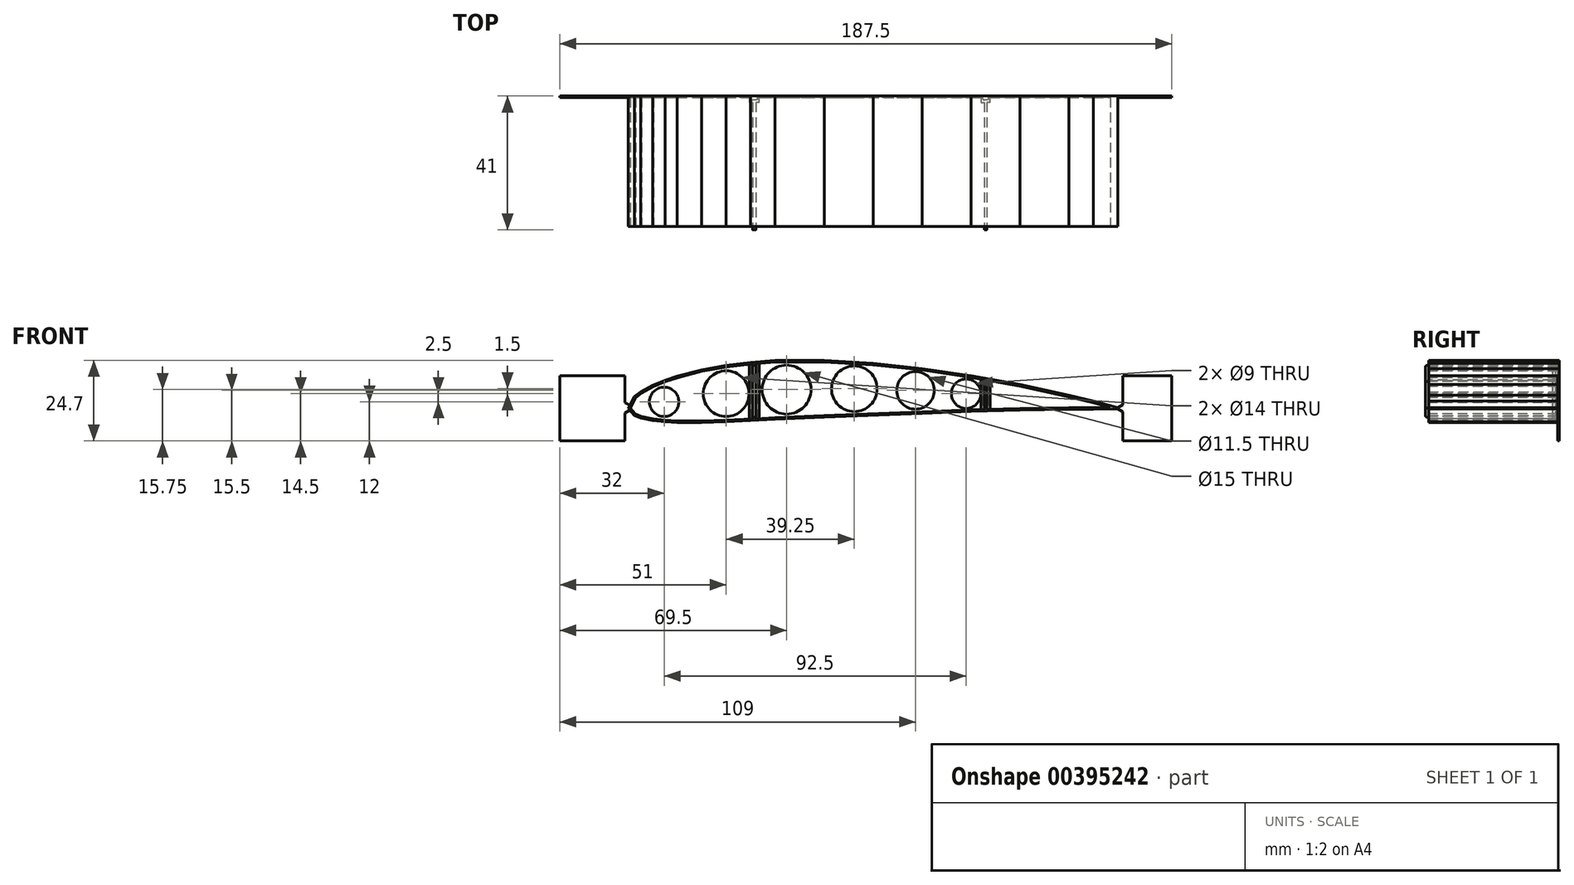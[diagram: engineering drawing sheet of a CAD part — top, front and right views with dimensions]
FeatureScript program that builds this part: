
annotation { "Feature Type Name" : "Feature", "Feature Type Description" : "" }
export const myFeature = defineFeature(function(context is Context, id is Id, definition is map)
    precondition{}
    {
        {
            var Q0;
            Q0=qCreatedBy(makeId("Front.planeOp"),FACE);
            var sketch = newSketch(context, id + "F0", { "sketchPlane" : qUnion([Q0])});
            skLineSegment(sketch, "E0", {"start": v(150, 0.2) * mm, "end": v(142.5, 2.2) * mm});
            skLineSegment(sketch, "E1", {"start": v(142.5, 2.2) * mm, "end": v(135, 4.07) * mm});
            skLineSegment(sketch, "E2", {"start": v(135, 4.07) * mm, "end": v(120, 7.34) * mm});
            skLineSegment(sketch, "E3", {"start": v(120, 7.34) * mm, "end": v(105, 10.04) * mm});
            skLineSegment(sketch, "E4", {"start": v(105, 10.03) * mm, "end": v(90, 12.2) * mm});
            skLineSegment(sketch, "E5", {"start": v(90, 12.21) * mm, "end": v(75, 13.79) * mm});
            skLineSegment(sketch, "E6", {"start": v(75, 13.79) * mm, "end": v(60, 14.7) * mm});
            skLineSegment(sketch, "E7", {"start": v(60, 14.7) * mm, "end": v(45, 14.64) * mm});
            skLineSegment(sketch, "E8", {"start": v(45, 14.64) * mm, "end": v(37.5, 14.11) * mm});
            skLineSegment(sketch, "E9", {"start": v(37.5, 14.12) * mm, "end": v(30, 13.2) * mm});
            skLineSegment(sketch, "E10", {"start": v(30, 13.2) * mm, "end": v(22.5, 11.83) * mm});
            skLineSegment(sketch, "E11", {"start": v(22.5, 11.84) * mm, "end": v(15, 9.88) * mm});
            skLineSegment(sketch, "E12", {"start": v(15, 9.88) * mm, "end": v(11.25, 8.64) * mm});
            skLineSegment(sketch, "E13", {"start": v(0, 0) * mm, "end": v(1.88, -2.15) * mm});
            skLineSegment(sketch, "E14", {"start": v(1.87, -2.14) * mm, "end": v(3.75, -2.92) * mm});
            skLineSegment(sketch, "E15", {"start": v(3.75, -2.92) * mm, "end": v(7.5, -3.73) * mm});
            skLineSegment(sketch, "E16", {"start": v(7.5, -3.73) * mm, "end": v(11.25, -4.11) * mm});
            skLineSegment(sketch, "E17", {"start": v(11.25, -4.1) * mm, "end": v(15, -4.3) * mm});
            skLineSegment(sketch, "E18", {"start": v(15, -4.29) * mm, "end": v(22.5, -4.32) * mm});
            skLineSegment(sketch, "E19", {"start": v(22.5, -4.32) * mm, "end": v(30, -4.11) * mm});
            skLineSegment(sketch, "E20", {"start": v(30, -4.11) * mm, "end": v(37.5, -3.75) * mm});
            skLineSegment(sketch, "E21", {"start": v(37.5, -3.75) * mm, "end": v(45, -3.39) * mm});
            skLineSegment(sketch, "E22", {"start": v(45, -3.39) * mm, "end": v(60, -2.7) * mm});
            skLineSegment(sketch, "E23", {"start": v(60, -2.7) * mm, "end": v(75, -2.1) * mm});
            skLineSegment(sketch, "E24", {"start": v(75, -2.1) * mm, "end": v(90, -1.5) * mm});
            skLineSegment(sketch, "E25", {"start": v(11.25, 8.64) * mm, "end": v(7.5, 7.1) * mm});
            skLineSegment(sketch, "E26", {"start": v(7.5, 7.1) * mm, "end": v(3.75, 5.08) * mm});
            skLineSegment(sketch, "E27", {"start": v(3.75, 5.08) * mm, "end": v(1.88, 3.66) * mm});
            skLineSegment(sketch, "E28", {"start": v(1.88, 3.66) * mm, "end": v(0, 0) * mm});
            skLineSegment(sketch, "E29", {"start": v(90, -1.5) * mm, "end": v(105, -0.97) * mm});
            skLineSegment(sketch, "E30", {"start": v(105, -0.97) * mm, "end": v(120, -0.58) * mm});
            skLineSegment(sketch, "E31", {"start": v(120, -0.58) * mm, "end": v(135, -0.33) * mm});
            skLineSegment(sketch, "E32", {"start": v(135, -0.33) * mm, "end": v(142.5, -0.24) * mm});
            skLineSegment(sketch, "E33", {"start": v(142.5, -0.24) * mm, "end": v(150, -0.2) * mm});
            skLineSegment(sketch, "E34", {"start": v(150, -0.2) * mm, "end": v(150, 0.2) * mm});
            skSolve(sketch);
        }
        {
            var Q0;
            Q0=makeQuery(id+"F0.imprint","IMPRINT",FACE,{"disambiguationData":[TD([[makeQuery(id+"F0.imprint","IMPRINT",EDGE,{"derivedFrom":sQuery(id+"F0.wireOp",EDGE,"E0")}),1.0]])]});
            extrude(context, id + "F1", {"entities" : qUnion([Q0]), "depth" : 40 * mm});
        }
        {
            var Q0;
            Q0=makeQuery(id+"F1.opExtrude","CAP_FACE",FACE,{"disambiguationData":[OSD([sQuery(id+"F0.wireOp",EDGE,"E0"),sQuery(id+"F0.wireOp",EDGE,"E1"),sQuery(id+"F0.wireOp",EDGE,"E2"),sQuery(id+"F0.wireOp",EDGE,"E3"),sQuery(id+"F0.wireOp",EDGE,"E4"),sQuery(id+"F0.wireOp",EDGE,"E5"),sQuery(id+"F0.wireOp",EDGE,"E6"),sQuery(id+"F0.wireOp",EDGE,"E7"),sQuery(id+"F0.wireOp",EDGE,"E8"),sQuery(id+"F0.wireOp",EDGE,"E9"),sQuery(id+"F0.wireOp",EDGE,"E10"),sQuery(id+"F0.wireOp",EDGE,"E11"),sQuery(id+"F0.wireOp",EDGE,"E12"),sQuery(id+"F0.wireOp",EDGE,"E13"),sQuery(id+"F0.wireOp",EDGE,"E14"),sQuery(id+"F0.wireOp",EDGE,"E15"),sQuery(id+"F0.wireOp",EDGE,"E16"),sQuery(id+"F0.wireOp",EDGE,"E17"),sQuery(id+"F0.wireOp",EDGE,"E18"),sQuery(id+"F0.wireOp",EDGE,"E19"),sQuery(id+"F0.wireOp",EDGE,"E20"),sQuery(id+"F0.wireOp",EDGE,"E21"),sQuery(id+"F0.wireOp",EDGE,"E22"),sQuery(id+"F0.wireOp",EDGE,"E23"),sQuery(id+"F0.wireOp",EDGE,"E24"),sQuery(id+"F0.wireOp",EDGE,"E25"),sQuery(id+"F0.wireOp",EDGE,"E26"),sQuery(id+"F0.wireOp",EDGE,"E27"),sQuery(id+"F0.wireOp",EDGE,"E28"),sQuery(id+"F0.wireOp",EDGE,"E29"),sQuery(id+"F0.wireOp",EDGE,"E30"),sQuery(id+"F0.wireOp",EDGE,"E31"),sQuery(id+"F0.wireOp",EDGE,"E32"),sQuery(id+"F0.wireOp",EDGE,"E33"),sQuery(id+"F0.wireOp",EDGE,"E34")])],"isStart":false});
            var sketch = newSketch(context, id + "F2", { "sketchPlane" : qUnion([Q0])});
            skLineSegment(sketch, "E35.0", {"start": v(119.99, -0.09) * mm, "end": v(135, 0.17) * mm});
            skLineSegment(sketch, "E35.1", {"start": v(104.98, -0.48) * mm, "end": v(109.1, -0.37) * mm});
            skLineSegment(sketch, "E35.2", {"start": v(89.98, -1) * mm, "end": v(104.98, -0.48) * mm});
            skLineSegment(sketch, "E35.3", {"start": v(59.98, -2.2) * mm, "end": v(89.98, -1) * mm});
            skLineSegment(sketch, "E35.4", {"start": v(44.98, -2.9) * mm, "end": v(59.98, -2.2) * mm});
            skLineSegment(sketch, "E35.5", {"start": v(29.98, -3.61) * mm, "end": v(38.1, -3.22) * mm});
            skLineSegment(sketch, "E35.6", {"start": v(22.5, -3.82) * mm, "end": v(29.98, -3.61) * mm});
            skLineSegment(sketch, "E35.7", {"start": v(15.01, -3.8) * mm, "end": v(22.5, -3.82) * mm});
            skLineSegment(sketch, "E35.8", {"start": v(11.29, -3.61) * mm, "end": v(15.01, -3.8) * mm});
            skLineSegment(sketch, "E35.9", {"start": v(45.02, 14.14) * mm, "end": v(39.1, 13.73) * mm});
            skLineSegment(sketch, "E35.10", {"start": v(59.99, 14.2) * mm, "end": v(45.02, 14.14) * mm});
            skLineSegment(sketch, "E35.11", {"start": v(74.96, 13.29) * mm, "end": v(59.99, 14.2) * mm});
            skLineSegment(sketch, "E35.12", {"start": v(89.94, 11.71) * mm, "end": v(74.96, 13.29) * mm});
            skLineSegment(sketch, "E35.13", {"start": v(104.92, 9.54) * mm, "end": v(89.94, 11.71) * mm});
            skLineSegment(sketch, "E35.14", {"start": v(119.9, 6.84) * mm, "end": v(109.85, 8.65) * mm});
            skLineSegment(sketch, "E35.15", {"start": v(142.5, 0.26) * mm, "end": v(147.7, 0.3) * mm});
            skLineSegment(sketch, "E35.16", {"start": v(147.7, 0.3) * mm, "end": v(142.38, 1.72) * mm});
            skLineSegment(sketch, "E35.17", {"start": v(142.38, 1.72) * mm, "end": v(134.89, 3.58) * mm});
            skLineSegment(sketch, "E35.18", {"start": v(134.89, 3.58) * mm, "end": v(119.9, 6.84) * mm});
            skLineSegment(sketch, "E35.19", {"start": v(37.55, 13.62) * mm, "end": v(30.08, 12.7) * mm});
            skLineSegment(sketch, "E35.20", {"start": v(30.08, 12.7) * mm, "end": v(22.6, 11.35) * mm});
            skLineSegment(sketch, "E35.21", {"start": v(22.6, 11.35) * mm, "end": v(15.14, 9.4) * mm});
            skLineSegment(sketch, "E35.22", {"start": v(15.14, 9.4) * mm, "end": v(11.42, 8.17) * mm});
            skLineSegment(sketch, "E35.23", {"start": v(11.42, 8.17) * mm, "end": v(7.71, 6.64) * mm});
            skLineSegment(sketch, "E35.24", {"start": v(7.71, 6.64) * mm, "end": v(4.02, 4.66) * mm});
            skLineSegment(sketch, "E35.25", {"start": v(4.02, 4.66) * mm, "end": v(2.27, 3.33) * mm});
            skLineSegment(sketch, "E35.26", {"start": v(2.27, 3.33) * mm, "end": v(0.6, 0.07) * mm});
            skLineSegment(sketch, "E35.27", {"start": v(0.6, 0.07) * mm, "end": v(2.17, -1.73) * mm});
            skLineSegment(sketch, "E35.28", {"start": v(135, 0.17) * mm, "end": v(142.5, 0.26) * mm});
            skLineSegment(sketch, "E35.29", {"start": v(2.17, -1.73) * mm, "end": v(3.9, -2.45) * mm});
            skLineSegment(sketch, "E35.30", {"start": v(3.9, -2.45) * mm, "end": v(7.58, -3.24) * mm});
            skLineSegment(sketch, "E35.31", {"start": v(7.58, -3.24) * mm, "end": v(11.29, -3.61) * mm});
            skLineSegment(sketch, "E36", {"start": v(0.6, 0.07) * mm, "end": v(38.1, 0.07) * mm, "construction": true});
            skLineSegment(sketch, "E37", {"start": v(38.1, -3.22) * mm, "end": v(38.1, 13.66) * mm});
            skLineSegment(sketch, "E38", {"start": v(39.1, -3.17) * mm, "end": v(39.1, 13.73) * mm});
            skLineSegment(sketch, "E39.trimOffspring", {"start": v(38.1, 13.66) * mm, "end": v(37.55, 13.62) * mm});
            skLineSegment(sketch, "E40.trimOffspring", {"start": v(39.1, -3.17) * mm, "end": v(44.98, -2.9) * mm});
            skLineSegment(sketch, "E41", {"start": v(39.1, 0) * mm, "end": v(109.1, 1.2) * mm, "construction": true});
            skLineSegment(sketch, "E42", {"start": v(109.1, 8.79) * mm, "end": v(109.1, -0.37) * mm});
            skLineSegment(sketch, "E43", {"start": v(109.85, -0.35) * mm, "end": v(109.85, 8.65) * mm});
            skLineSegment(sketch, "E44.trimOffspring", {"start": v(109.1, 8.79) * mm, "end": v(104.92, 9.54) * mm});
            skLineSegment(sketch, "E45.trimOffspring", {"start": v(109.85, -0.35) * mm, "end": v(119.99, -0.09) * mm});
            skSolve(sketch);
        }
        {
            var Q0;
            Q0=makeQuery(id+"F2.imprint","IMPRINT",FACE,{"disambiguationData":[TD([[makeQuery(id+"F2.imprint","IMPRINT",EDGE,{"derivedFrom":sQuery(id+"F2.wireOp",EDGE,"E35.5")}),1.0]])]});
            var Q1;
            Q1=makeQuery(id+"F2.imprint","IMPRINT",FACE,{"disambiguationData":[TD([[makeQuery(id+"F2.imprint","IMPRINT",EDGE,{"derivedFrom":sQuery(id+"F2.wireOp",EDGE,"E35.1")}),1.0]])]});
            var Q2;
            Q2=makeQuery(id+"F2.imprint","IMPRINT",FACE,{"disambiguationData":[TD([[makeQuery(id+"F2.imprint","IMPRINT",EDGE,{"derivedFrom":sQuery(id+"F2.wireOp",EDGE,"E35.0")}),1.0]])]});
            extrude(context, id + "F3", {"entities" : qUnion([Q0, Q1, Q2]), "operationType" : NewBodyOperationType.REMOVE, "oppositeDirection" : true, "depth" : 39.5 * mm});
        }
        {
            var Q0;
            Q0=makeQuery(id+"F3.boolean.opBoolean","COPY",FACE,{"derivedFrom":makeQuery(id+"F3.opExtrude","CAP_FACE",FACE,{"disambiguationData":[OSD([sQuery(id+"F2.wireOp",EDGE,"E35.1"),sQuery(id+"F2.wireOp",EDGE,"E35.2"),sQuery(id+"F2.wireOp",EDGE,"E35.3"),sQuery(id+"F2.wireOp",EDGE,"E35.4"),sQuery(id+"F2.wireOp",EDGE,"E35.9"),sQuery(id+"F2.wireOp",EDGE,"E35.10"),sQuery(id+"F2.wireOp",EDGE,"E35.11"),sQuery(id+"F2.wireOp",EDGE,"E35.12"),sQuery(id+"F2.wireOp",EDGE,"E35.13"),sQuery(id+"F2.wireOp",EDGE,"E38"),sQuery(id+"F2.wireOp",EDGE,"E40.trimOffspring"),sQuery(id+"F2.wireOp",EDGE,"E42"),sQuery(id+"F2.wireOp",EDGE,"E44.trimOffspring")])],"isStart":false})});
            var sketch = newSketch(context, id + "F4", { "sketchPlane" : qUnion([Q0])});
            skCircle(sketch, "E46", {"center": v(48.5, 5.75) * mm, "radius": 7.5 * mm});
            skCircle(sketch, "E47", {"center": v(69.25, 6) * mm, "radius": 7 * mm});
            skCircle(sketch, "E48", {"center": v(88, 5.5) * mm, "radius": 5.75 * mm});
            skCircle(sketch, "E49", {"center": v(103.5, 4.5) * mm, "radius": 4.5 * mm});
            skCircle(sketch, "E50", {"center": v(30, 4.5) * mm, "radius": 7 * mm});
            skCircle(sketch, "E51", {"center": v(11, 2) * mm, "radius": 4.5 * mm});
            skSolve(sketch);
        }
        {
            var Q0;
            Q0=makeQuery(id+"F4.imprint","IMPRINT",FACE,{"disambiguationData":[TD([[makeQuery(id+"F4.imprint","IMPRINT",EDGE,{"derivedFrom":sQuery(id+"F4.wireOp",EDGE,"E51")}),1.0]])]});
            var Q1;
            Q1=makeQuery(id+"F4.imprint","IMPRINT",FACE,{"disambiguationData":[TD([[makeQuery(id+"F4.imprint","IMPRINT",EDGE,{"derivedFrom":sQuery(id+"F4.wireOp",EDGE,"E50")}),1.0]])]});
            var Q2;
            Q2=makeQuery(id+"F4.imprint","IMPRINT",FACE,{"disambiguationData":[TD([[makeQuery(id+"F4.imprint","IMPRINT",EDGE,{"derivedFrom":sQuery(id+"F4.wireOp",EDGE,"E46")}),1.0]])]});
            var Q3;
            Q3=makeQuery(id+"F4.imprint","IMPRINT",FACE,{"disambiguationData":[TD([[makeQuery(id+"F4.imprint","IMPRINT",EDGE,{"derivedFrom":sQuery(id+"F4.wireOp",EDGE,"E47")}),1.0]])]});
            var Q4;
            Q4=makeQuery(id+"F4.imprint","IMPRINT",FACE,{"disambiguationData":[TD([[makeQuery(id+"F4.imprint","IMPRINT",EDGE,{"derivedFrom":sQuery(id+"F4.wireOp",EDGE,"E48")}),1.0]])]});
            var Q5;
            Q5=makeQuery(id+"F4.imprint","IMPRINT",FACE,{"disambiguationData":[TD([[makeQuery(id+"F4.imprint","IMPRINT",EDGE,{"derivedFrom":sQuery(id+"F4.wireOp",EDGE,"E49")}),1.0]])]});
            extrude(context, id + "F5", {"entities" : qUnion([Q0, Q1, Q2, Q3, Q4, Q5]), "operationType" : NewBodyOperationType.REMOVE, "endBound" : BoundingType.THROUGH_ALL, "oppositeDirection" : true, "depth" : 25 * mm});
        }
        {
            var Q0;
            Q0=makeQuery(id+"F1.opExtrude","CAP_FACE",FACE,{"disambiguationData":[OSD([sQuery(id+"F0.wireOp",EDGE,"E0"),sQuery(id+"F0.wireOp",EDGE,"E1"),sQuery(id+"F0.wireOp",EDGE,"E2"),sQuery(id+"F0.wireOp",EDGE,"E3"),sQuery(id+"F0.wireOp",EDGE,"E4"),sQuery(id+"F0.wireOp",EDGE,"E5"),sQuery(id+"F0.wireOp",EDGE,"E6"),sQuery(id+"F0.wireOp",EDGE,"E7"),sQuery(id+"F0.wireOp",EDGE,"E8"),sQuery(id+"F0.wireOp",EDGE,"E9"),sQuery(id+"F0.wireOp",EDGE,"E10"),sQuery(id+"F0.wireOp",EDGE,"E11"),sQuery(id+"F0.wireOp",EDGE,"E12"),sQuery(id+"F0.wireOp",EDGE,"E13"),sQuery(id+"F0.wireOp",EDGE,"E14"),sQuery(id+"F0.wireOp",EDGE,"E15"),sQuery(id+"F0.wireOp",EDGE,"E16"),sQuery(id+"F0.wireOp",EDGE,"E17"),sQuery(id+"F0.wireOp",EDGE,"E18"),sQuery(id+"F0.wireOp",EDGE,"E19"),sQuery(id+"F0.wireOp",EDGE,"E20"),sQuery(id+"F0.wireOp",EDGE,"E21"),sQuery(id+"F0.wireOp",EDGE,"E22"),sQuery(id+"F0.wireOp",EDGE,"E23"),sQuery(id+"F0.wireOp",EDGE,"E24"),sQuery(id+"F0.wireOp",EDGE,"E25"),sQuery(id+"F0.wireOp",EDGE,"E26"),sQuery(id+"F0.wireOp",EDGE,"E27"),sQuery(id+"F0.wireOp",EDGE,"E28"),sQuery(id+"F0.wireOp",EDGE,"E29"),sQuery(id+"F0.wireOp",EDGE,"E30"),sQuery(id+"F0.wireOp",EDGE,"E31"),sQuery(id+"F0.wireOp",EDGE,"E32"),sQuery(id+"F0.wireOp",EDGE,"E33"),sQuery(id+"F0.wireOp",EDGE,"E34")])],"isStart":true});
            var sketch = newSketch(context, id + "F6", { "sketchPlane" : qUnion([Q0])});
            skLineSegment(sketch, "E52.left", {"start": v(-37.1, 14.07) * mm, "end": v(-37.1, -3.77) * mm});
            skLineSegment(sketch, "E52.right", {"start": v(-40.1, 14.3) * mm, "end": v(-40.1, -3.63) * mm});
            skLineSegment(sketch, "E53.left", {"start": v(-108.1, 9.48) * mm, "end": v(-108.1, -0.9) * mm});
            skLineSegment(sketch, "E53.right", {"start": v(-110.85, 8.98) * mm, "end": v(-110.85, -0.82) * mm});
            skLineSegment(sketch, "E54", {"start": v(-40.1, 14.3) * mm, "end": v(-37.5, 14.11) * mm});
            skLineSegment(sketch, "E55", {"start": v(-37.5, 14.12) * mm, "end": v(-37.1, 14.07) * mm});
            skLineSegment(sketch, "E56", {"start": v(-37.1, -3.77) * mm, "end": v(-40.1, -3.63) * mm});
            skLineSegment(sketch, "E57", {"start": v(-110.85, 8.98) * mm, "end": v(-108.1, 9.48) * mm});
            skLineSegment(sketch, "E58", {"start": v(-108.1, -0.9) * mm, "end": v(-110.85, -0.82) * mm});
            skSolve(sketch);
        }
        {
            var Q0;
            Q0=makeQuery(id+"F6.imprint","IMPRINT",FACE,{"disambiguationData":[TD([[makeQuery(id+"F6.imprint","IMPRINT",EDGE,{"derivedFrom":sQuery(id+"F6.wireOp",EDGE,"E53.left")}),-1.0]])]});
            var Q1;
            Q1=makeQuery(id+"F6.imprint","IMPRINT",FACE,{"disambiguationData":[TD([[makeQuery(id+"F6.imprint","IMPRINT",EDGE,{"derivedFrom":sQuery(id+"F6.wireOp",EDGE,"E52.left")}),-1.0]])]});
            extrude(context, id + "F7", {"entities" : qUnion([Q0, Q1]), "operationType" : NewBodyOperationType.ADD, "oppositeDirection" : true, "depth" : 2 * mm});
        }
        {
            var Q0;
            {var subQ8=sQuery(id+"F6.wireOp",EDGE,"E52.right");Q0=makeQuery(id+"F6.imprint","IMPRINT",FACE,{"disambiguationData":[TD([[makeQuery(id+"F6.imprint","IMPRINT",EDGE,{"derivedFrom":subQ8}),-1.0]])]});}
            var sketch = newSketch(context, id + "F8", { "sketchPlane" : qUnion([Q0])});
            skLineSegment(sketch, "E59.bottom", {"start": v(-110.35, 8.48) * mm, "end": v(-108.6, 8.48) * mm});
            skLineSegment(sketch, "E59.top", {"start": v(-110.35, -0.32) * mm, "end": v(-108.6, -0.32) * mm});
            skLineSegment(sketch, "E59.left", {"start": v(-110.35, 8.48) * mm, "end": v(-110.35, -0.32) * mm});
            skLineSegment(sketch, "E59.right", {"start": v(-108.6, 8.48) * mm, "end": v(-108.6, -0.32) * mm});
            skLineSegment(sketch, "E60.bottom", {"start": v(-39.6, 13.57) * mm, "end": v(-37.6, 13.57) * mm});
            skLineSegment(sketch, "E60.top", {"start": v(-39.6, -3.13) * mm, "end": v(-37.6, -3.13) * mm});
            skLineSegment(sketch, "E60.left", {"start": v(-39.6, 13.57) * mm, "end": v(-39.6, -3.13) * mm});
            skLineSegment(sketch, "E60.right", {"start": v(-37.6, 13.57) * mm, "end": v(-37.6, -3.13) * mm});
            skSolve(sketch);
        }
        {
            var Q0;
            Q0=makeQuery(id+"F8.imprint","IMPRINT",FACE,{"disambiguationData":[TD([[makeQuery(id+"F8.imprint","IMPRINT",EDGE,{"derivedFrom":sQuery(id+"F8.wireOp",EDGE,"E59.bottom")}),-1.0]])]});
            var Q1;
            Q1=makeQuery(id+"F8.imprint","IMPRINT",FACE,{"disambiguationData":[TD([[makeQuery(id+"F8.imprint","IMPRINT",EDGE,{"derivedFrom":sQuery(id+"F8.wireOp",EDGE,"E60.bottom")}),-1.0]])]});
            extrude(context, id + "F9", {"entities" : qUnion([Q0, Q1]), "operationType" : NewBodyOperationType.REMOVE, "oppositeDirection" : true, "depth" : 1.25 * mm});
        }
        {
            var Q0;
            Q0=makeQuery(id+"F9.boolean.opBoolean","COPY",FACE,{"derivedFrom":makeQuery(id+"F9.opExtrude","CAP_FACE",FACE,{"disambiguationData":[OSD([sQuery(id+"F8.wireOp",EDGE,"E60.bottom"),sQuery(id+"F8.wireOp",EDGE,"E60.top"),sQuery(id+"F8.wireOp",EDGE,"E60.left"),sQuery(id+"F8.wireOp",EDGE,"E60.right")])],"isStart":false})});
            var Q1;
            Q1=makeQuery(id+"F9.boolean.opBoolean","COPY",FACE,{"derivedFrom":makeQuery(id+"F9.opExtrude","CAP_FACE",FACE,{"disambiguationData":[OSD([sQuery(id+"F8.wireOp",EDGE,"E59.bottom"),sQuery(id+"F8.wireOp",EDGE,"E59.top"),sQuery(id+"F8.wireOp",EDGE,"E59.left"),sQuery(id+"F8.wireOp",EDGE,"E59.right")])],"isStart":false})});
            fillet(context, id + "F10", {"entities" : qUnion([Q0, Q1]), "radius" : 0.5 * mm, "tangentPropagation" : true, "allowEdgeOverflow" : false});
        }
        {
            var Q0;
            Q0=makeQuery(id+"F1.opExtrude","CAP_FACE",FACE,{"disambiguationData":[OSD([sQuery(id+"F0.wireOp",EDGE,"E0"),sQuery(id+"F0.wireOp",EDGE,"E1"),sQuery(id+"F0.wireOp",EDGE,"E2"),sQuery(id+"F0.wireOp",EDGE,"E3"),sQuery(id+"F0.wireOp",EDGE,"E4"),sQuery(id+"F0.wireOp",EDGE,"E5"),sQuery(id+"F0.wireOp",EDGE,"E6"),sQuery(id+"F0.wireOp",EDGE,"E7"),sQuery(id+"F0.wireOp",EDGE,"E8"),sQuery(id+"F0.wireOp",EDGE,"E9"),sQuery(id+"F0.wireOp",EDGE,"E10"),sQuery(id+"F0.wireOp",EDGE,"E11"),sQuery(id+"F0.wireOp",EDGE,"E12"),sQuery(id+"F0.wireOp",EDGE,"E13"),sQuery(id+"F0.wireOp",EDGE,"E14"),sQuery(id+"F0.wireOp",EDGE,"E15"),sQuery(id+"F0.wireOp",EDGE,"E16"),sQuery(id+"F0.wireOp",EDGE,"E17"),sQuery(id+"F0.wireOp",EDGE,"E18"),sQuery(id+"F0.wireOp",EDGE,"E19"),sQuery(id+"F0.wireOp",EDGE,"E20"),sQuery(id+"F0.wireOp",EDGE,"E21"),sQuery(id+"F0.wireOp",EDGE,"E22"),sQuery(id+"F0.wireOp",EDGE,"E23"),sQuery(id+"F0.wireOp",EDGE,"E24"),sQuery(id+"F0.wireOp",EDGE,"E25"),sQuery(id+"F0.wireOp",EDGE,"E26"),sQuery(id+"F0.wireOp",EDGE,"E27"),sQuery(id+"F0.wireOp",EDGE,"E28"),sQuery(id+"F0.wireOp",EDGE,"E29"),sQuery(id+"F0.wireOp",EDGE,"E30"),sQuery(id+"F0.wireOp",EDGE,"E31"),sQuery(id+"F0.wireOp",EDGE,"E32"),sQuery(id+"F0.wireOp",EDGE,"E33"),sQuery(id+"F0.wireOp",EDGE,"E34")])],"isStart":false});
            var sketch = newSketch(context, id + "F11", { "sketchPlane" : qUnion([Q0])});
            skLineSegment(sketch, "E61.bottom", {"start": v(39.1, 13.16) * mm, "end": v(38.1, 13.16) * mm});
            skLineSegment(sketch, "E61.top", {"start": v(39.1, -2.67) * mm, "end": v(38.1, -2.67) * mm});
            skLineSegment(sketch, "E61.left", {"start": v(39.1, 13.16) * mm, "end": v(39.1, -2.67) * mm});
            skLineSegment(sketch, "E61.right", {"start": v(38.1, 13.16) * mm, "end": v(38.1, -2.67) * mm});
            skLineSegment(sketch, "E62.bottom", {"start": v(109.85, 8.16) * mm, "end": v(109.1, 8.16) * mm});
            skLineSegment(sketch, "E62.top", {"start": v(109.85, 0.15) * mm, "end": v(109.1, 0.15) * mm});
            skLineSegment(sketch, "E62.left", {"start": v(109.85, 8.16) * mm, "end": v(109.85, 0.15) * mm});
            skLineSegment(sketch, "E62.right", {"start": v(109.1, 8.16) * mm, "end": v(109.1, 0.15) * mm});
            skPoint(sketch, "E63", {"position": v(109.85, 9.16) * mm});
            skPoint(sketch, "E64", {"position": v(109.85, -0.85) * mm});
            skPoint(sketch, "E65", {"position": v(38.1, 14.16) * mm});
            skPoint(sketch, "E66", {"position": v(39.1, -3.67) * mm});
            skSolve(sketch);
        }
        {
            var Q0;
            Q0=makeQuery(id+"F11.imprint","IMPRINT",FACE,{"disambiguationData":[TD([[makeQuery(id+"F11.imprint","IMPRINT",EDGE,{"derivedFrom":sQuery(id+"F11.wireOp",EDGE,"E62.bottom")}),1.0]])]});
            var Q1;
            Q1=makeQuery(id+"F11.imprint","IMPRINT",FACE,{"disambiguationData":[TD([[makeQuery(id+"F11.imprint","IMPRINT",EDGE,{"derivedFrom":sQuery(id+"F11.wireOp",EDGE,"E61.bottom")}),1.0]])]});
            extrude(context, id + "F12", {"entities" : qUnion([Q0, Q1]), "operationType" : NewBodyOperationType.ADD, "depth" : 1 * mm});
        }
        {
            var Q0;
            Q0=makeQuery(id+"F12.opExtrude","CAP_EDGE",EDGE,{"disambiguationData":[OSD([sQuery(id+"F11.wireOp",EDGE,"E61.bottom")])],"isStart":false});
            var Q1;
            Q1=makeQuery(id+"F12.opExtrude","CAP_EDGE",EDGE,{"disambiguationData":[OSD([sQuery(id+"F11.wireOp",EDGE,"E61.top")])],"isStart":false});
            var Q2;
            Q2=makeQuery(id+"F12.opExtrude","CAP_EDGE",EDGE,{"disambiguationData":[OSD([sQuery(id+"F11.wireOp",EDGE,"E62.top")])],"isStart":false});
            var Q3;
            Q3=makeQuery(id+"F12.opExtrude","CAP_EDGE",EDGE,{"disambiguationData":[OSD([sQuery(id+"F11.wireOp",EDGE,"E62.bottom")])],"isStart":false});
            fillet(context, id + "F13", {"entities" : qUnion([Q0, Q1, Q2, Q3]), "radius" : 0.5 * mm, "tangentPropagation" : true, "allowEdgeOverflow" : false});
        }
        {
            var Q0;
            Q0=makeQuery(id+"F1.opExtrude","CAP_FACE",FACE,{"disambiguationData":[OSD([sQuery(id+"F0.wireOp",EDGE,"E0"),sQuery(id+"F0.wireOp",EDGE,"E1"),sQuery(id+"F0.wireOp",EDGE,"E2"),sQuery(id+"F0.wireOp",EDGE,"E3"),sQuery(id+"F0.wireOp",EDGE,"E4"),sQuery(id+"F0.wireOp",EDGE,"E5"),sQuery(id+"F0.wireOp",EDGE,"E6"),sQuery(id+"F0.wireOp",EDGE,"E7"),sQuery(id+"F0.wireOp",EDGE,"E8"),sQuery(id+"F0.wireOp",EDGE,"E9"),sQuery(id+"F0.wireOp",EDGE,"E10"),sQuery(id+"F0.wireOp",EDGE,"E11"),sQuery(id+"F0.wireOp",EDGE,"E12"),sQuery(id+"F0.wireOp",EDGE,"E13"),sQuery(id+"F0.wireOp",EDGE,"E14"),sQuery(id+"F0.wireOp",EDGE,"E15"),sQuery(id+"F0.wireOp",EDGE,"E16"),sQuery(id+"F0.wireOp",EDGE,"E17"),sQuery(id+"F0.wireOp",EDGE,"E18"),sQuery(id+"F0.wireOp",EDGE,"E19"),sQuery(id+"F0.wireOp",EDGE,"E20"),sQuery(id+"F0.wireOp",EDGE,"E21"),sQuery(id+"F0.wireOp",EDGE,"E22"),sQuery(id+"F0.wireOp",EDGE,"E23"),sQuery(id+"F0.wireOp",EDGE,"E24"),sQuery(id+"F0.wireOp",EDGE,"E25"),sQuery(id+"F0.wireOp",EDGE,"E26"),sQuery(id+"F0.wireOp",EDGE,"E27"),sQuery(id+"F0.wireOp",EDGE,"E28"),sQuery(id+"F0.wireOp",EDGE,"E29"),sQuery(id+"F0.wireOp",EDGE,"E30"),sQuery(id+"F0.wireOp",EDGE,"E31"),sQuery(id+"F0.wireOp",EDGE,"E32"),sQuery(id+"F0.wireOp",EDGE,"E33"),sQuery(id+"F0.wireOp",EDGE,"E34")])],"isStart":true});
            var sketch = newSketch(context, id + "F14", { "sketchPlane" : qUnion([Q0])});
            skLineSegment(sketch, "E67.bottom", {"start": v(1, 10) * mm, "end": v(21, 10) * mm});
            skLineSegment(sketch, "E67.top", {"start": v(1, -10) * mm, "end": v(21, -10) * mm});
            skLineSegment(sketch, "E67.left", {"start": v(1, 10) * mm, "end": v(1, 1.8) * mm});
            skLineSegment(sketch, "E67.right", {"start": v(21, 10) * mm, "end": v(21, -10) * mm});
            skLineSegment(sketch, "E68", {"start": v(-0.48, -0.55) * mm, "end": v(1, -1.41) * mm});
            skLineSegment(sketch, "E69", {"start": v(-0.48, -0.55) * mm, "end": v(0, 0) * mm});
            skLineSegment(sketch, "E70", {"start": v(0, 0) * mm, "end": v(-0.48, 0.95) * mm});
            skLineSegment(sketch, "E71", {"start": v(-0.48, 0.95) * mm, "end": v(1, 1.8) * mm});
            skLineSegment(sketch, "E72.trimOffspring", {"start": v(1, -1.41) * mm, "end": v(1, -10) * mm});
            skSolve(sketch);
        }
        {
            var Q0;
            Q0=makeQuery(id+"F14.imprint","IMPRINT",FACE,{"disambiguationData":[TD([[makeQuery(id+"F14.imprint","IMPRINT",EDGE,{"derivedFrom":sQuery(id+"F14.wireOp",EDGE,"E67.bottom")}),-1.0]])]});
            extrude(context, id + "F15", {"entities" : qUnion([Q0]), "operationType" : NewBodyOperationType.ADD, "oppositeDirection" : true, "depth" : 0.5 * mm});
        }
        {
            var Q0;
            Q0=makeQuery(id+"F15.boolean.opBoolean","MERGE",FACE,{"derivedFrom":[makeQuery(id+"F1.opExtrude","CAP_FACE",FACE,{"disambiguationData":[OSD([sQuery(id+"F0.wireOp",EDGE,"E0"),sQuery(id+"F0.wireOp",EDGE,"E1"),sQuery(id+"F0.wireOp",EDGE,"E2"),sQuery(id+"F0.wireOp",EDGE,"E3"),sQuery(id+"F0.wireOp",EDGE,"E4"),sQuery(id+"F0.wireOp",EDGE,"E5"),sQuery(id+"F0.wireOp",EDGE,"E6"),sQuery(id+"F0.wireOp",EDGE,"E7"),sQuery(id+"F0.wireOp",EDGE,"E8"),sQuery(id+"F0.wireOp",EDGE,"E9"),sQuery(id+"F0.wireOp",EDGE,"E10"),sQuery(id+"F0.wireOp",EDGE,"E11"),sQuery(id+"F0.wireOp",EDGE,"E12"),sQuery(id+"F0.wireOp",EDGE,"E13"),sQuery(id+"F0.wireOp",EDGE,"E14"),sQuery(id+"F0.wireOp",EDGE,"E15"),sQuery(id+"F0.wireOp",EDGE,"E16"),sQuery(id+"F0.wireOp",EDGE,"E17"),sQuery(id+"F0.wireOp",EDGE,"E18"),sQuery(id+"F0.wireOp",EDGE,"E19"),sQuery(id+"F0.wireOp",EDGE,"E20"),sQuery(id+"F0.wireOp",EDGE,"E21"),sQuery(id+"F0.wireOp",EDGE,"E22"),sQuery(id+"F0.wireOp",EDGE,"E23"),sQuery(id+"F0.wireOp",EDGE,"E24"),sQuery(id+"F0.wireOp",EDGE,"E25"),sQuery(id+"F0.wireOp",EDGE,"E26"),sQuery(id+"F0.wireOp",EDGE,"E27"),sQuery(id+"F0.wireOp",EDGE,"E28"),sQuery(id+"F0.wireOp",EDGE,"E29"),sQuery(id+"F0.wireOp",EDGE,"E30"),sQuery(id+"F0.wireOp",EDGE,"E31"),sQuery(id+"F0.wireOp",EDGE,"E32"),sQuery(id+"F0.wireOp",EDGE,"E33"),sQuery(id+"F0.wireOp",EDGE,"E34")])],"isStart":true}),makeQuery(id+"F15.opExtrude","CAP_FACE",FACE,{"disambiguationData":[OSD([sQuery(id+"F14.wireOp",EDGE,"E67.bottom"),sQuery(id+"F14.wireOp",EDGE,"E67.top"),sQuery(id+"F14.wireOp",EDGE,"E67.left"),sQuery(id+"F14.wireOp",EDGE,"E67.right"),sQuery(id+"F14.wireOp",EDGE,"E68"),sQuery(id+"F14.wireOp",EDGE,"E69"),sQuery(id+"F14.wireOp",EDGE,"E70"),sQuery(id+"F14.wireOp",EDGE,"E71"),sQuery(id+"F14.wireOp",EDGE,"E72.trimOffspring")])],"isStart":true})]});
            var sketch = newSketch(context, id + "F16", { "sketchPlane" : qUnion([Q0])});
            skLineSegment(sketch, "E73.bottom", {"start": v(-151.5, 10) * mm, "end": v(-166.5, 10) * mm});
            skLineSegment(sketch, "E73.top", {"start": v(-151.5, -10) * mm, "end": v(-166.5, -10) * mm});
            skLineSegment(sketch, "E73.left", {"start": v(-151.5, 10) * mm, "end": v(-151.5, 1.06) * mm});
            skLineSegment(sketch, "E73.right", {"start": v(-166.5, 10) * mm, "end": v(-166.5, -10) * mm});
            skLineSegment(sketch, "E74", {"start": v(-150, -0.2) * mm, "end": v(-151.5, -1.06) * mm});
            skLineSegment(sketch, "E75", {"start": v(-150, -0.2) * mm, "end": v(-150, 0.2) * mm});
            skLineSegment(sketch, "E76", {"start": v(-150, 0.2) * mm, "end": v(-151.5, 1.06) * mm});
            skLineSegment(sketch, "E77.trimOffspring", {"start": v(-151.5, -1.06) * mm, "end": v(-151.5, -10) * mm});
            skSolve(sketch);
        }
        {
            var Q0;
            Q0=makeQuery(id+"F16.imprint","IMPRINT",FACE,{"disambiguationData":[TD([[makeQuery(id+"F16.imprint","IMPRINT",EDGE,{"derivedFrom":sQuery(id+"F16.wireOp",EDGE,"E73.bottom")}),1.0]])]});
            extrude(context, id + "F17", {"entities" : qUnion([Q0]), "operationType" : NewBodyOperationType.ADD, "oppositeDirection" : true, "depth" : 0.5 * mm});
        }
    });
